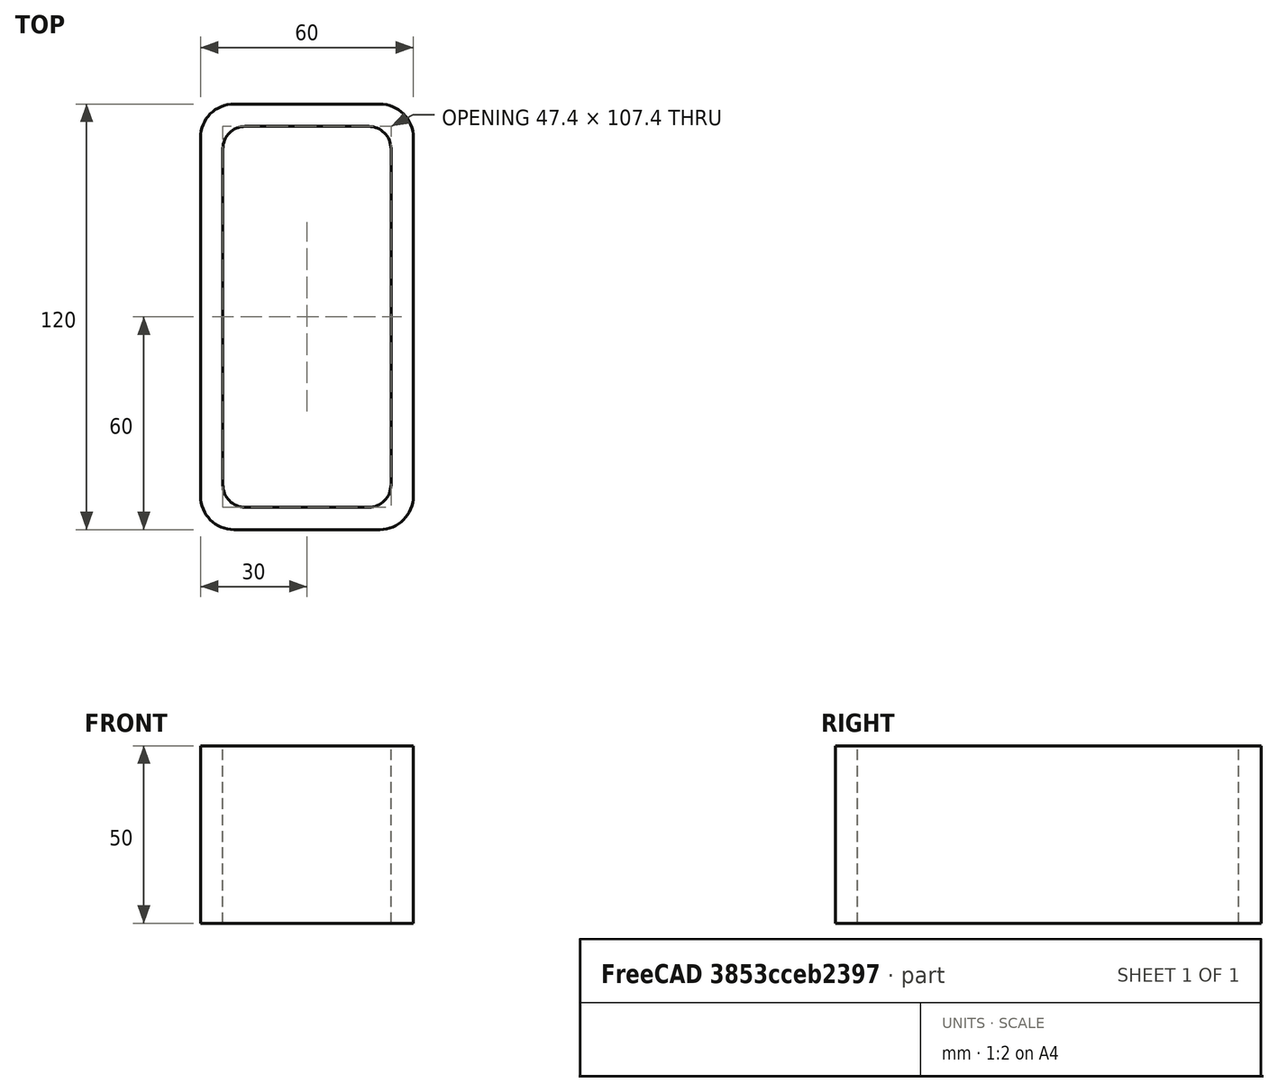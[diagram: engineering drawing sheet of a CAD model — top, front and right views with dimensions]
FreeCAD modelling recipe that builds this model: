
FCSTD DOCUMENT  (FreeCAD 0.15R4671 (Git))
Label: Rectangular hollow section 120x60x6.3 EN10219 S235JRH
License: All rights reserved
LicenseURL: http://en.wikipedia.org/wiki/All_rights_reserved
objects: Sketcher::SketchObject×1, Part::Extrusion×1
note: 2 computed .brp shape members not serialized (recipe doc carries the construction recipe); baked Part::Feature solids carry a one-line shape summary decoded from their .brp

FEATURE [Sketcher::SketchObject] Sketch
  sketch-geometry (16):
    g0: LineSegment StartX=-17.4 StartY=53.7 StartZ=0 EndX=17.4 EndY=53.7 EndZ=0
    g1: LineSegment StartX=23.7 StartY=47.4 StartZ=0 EndX=23.7 EndY=-47.4 EndZ=0
    g2: LineSegment StartX=17.4 StartY=-53.7 StartZ=0 EndX=-17.4 EndY=-53.7 EndZ=0
    g3: LineSegment StartX=-23.7 StartY=-47.4 StartZ=0 EndX=-23.7 EndY=47.4 EndZ=0
    g4: LineSegment StartX=-20.55 StartY=60 StartZ=0 EndX=20.55 EndY=60 EndZ=0
    g5: LineSegment StartX=30 StartY=50.55 StartZ=0 EndX=30 EndY=-50.55 EndZ=0
    g6: LineSegment StartX=20.55 StartY=-60 StartZ=0 EndX=-20.55 EndY=-60 EndZ=0
    g7: LineSegment StartX=-30 StartY=-50.55 StartZ=0 EndX=-30 EndY=50.55 EndZ=0
    g8: ArcOfCircle CenterX=-17.4 CenterY=47.4 CenterZ=0 NormalX=0 NormalY=0 NormalZ=1 Radius=6.3 StartAngle=1.5708 EndAngle=3.14159
    g9: ArcOfCircle CenterX=17.4 CenterY=47.4 CenterZ=0 NormalX=0 NormalY=0 NormalZ=1 Radius=6.3 StartAngle=0 EndAngle=1.5708
    g10: ArcOfCircle CenterX=17.4 CenterY=-47.4 CenterZ=0 NormalX=0 NormalY=0 NormalZ=1 Radius=6.3 StartAngle=4.71239 EndAngle=6.28319
    g11: ArcOfCircle CenterX=-17.4 CenterY=-47.4 CenterZ=0 NormalX=0 NormalY=0 NormalZ=1 Radius=6.3 StartAngle=3.14159 EndAngle=4.71239
    g12: ArcOfCircle CenterX=20.55 CenterY=50.55 CenterZ=0 NormalX=0 NormalY=0 NormalZ=1 Radius=9.45 StartAngle=0 EndAngle=1.5708
    g13: ArcOfCircle CenterX=20.55 CenterY=-50.55 CenterZ=0 NormalX=0 NormalY=0 NormalZ=1 Radius=9.45 StartAngle=4.71239 EndAngle=6.28319
    g14: ArcOfCircle CenterX=-20.55 CenterY=-50.55 CenterZ=0 NormalX=0 NormalY=0 NormalZ=1 Radius=9.45 StartAngle=3.14159 EndAngle=4.71239
    g15: ArcOfCircle CenterX=-20.55 CenterY=50.55 CenterZ=0 NormalX=0 NormalY=0 NormalZ=1 Radius=9.45 StartAngle=1.5708 EndAngle=3.14159
  constraints (36):
    c: Horizontal(g2)
    c: Vertical(g3)
    c: Horizontal(g6)
    c: Vertical(g7)
    c: Tangent(g3,g8) = 1.5708
    c: Tangent(g0,g8) = 1.5708
    c: Tangent(g0,g9) = 1.5708
    c: Tangent(g1,g9) = 1.5708
    c: Tangent(g1,g10) = 1.5708
    c: Tangent(g2,g10) = 1.5708
    c: Tangent(g2,g11) = 1.5708
    c: Tangent(g3,g11) = 1.5708
    c: Tangent(g4,g12) = 1.5708
    c: Tangent(g5,g12) = 1.5708
    c: Tangent(g5,g13) = 1.5708
    c: Tangent(g6,g13) = 1.5708
    c: Tangent(g6,g14) = 1.5708
    c: Tangent(g7,g14) = 1.5708
    c: Tangent(g7,g15) = 1.5708
    c: Tangent(g4,g15) = 1.5708
    c: Equal(g9,g8)
    c: Equal(g9,g11)
    c: Equal(g9,g10)
    c: Equal(g12,g15)
    c: Equal(g12,g14)
    c: Equal(g12,g13)
    c: Symmetric(g4,g6,g-1)
    c: Symmetric(g7,g5,g-2)
    c: DistanceY(g4,g6) = -120
    c: DistanceX(g7,g5) = 60
    c: Symmetric(g3,g1,g-2)
    c: Symmetric(g0,g2,g-1)
    c: DistanceY(g0,g4) = 6.3
    c: DistanceX(g5,g1) = -6.3
    c: Radius(g9) = 6.3
    c: Radius(g12) = 9.45
FEATURE [Part::Extrusion] Extrude  label="Rectangular hollow section 120x60x6.3 EN10219 S235JRH"
  Base = -> Sketch
  Dir = (0,0,50)
  Solid = true
